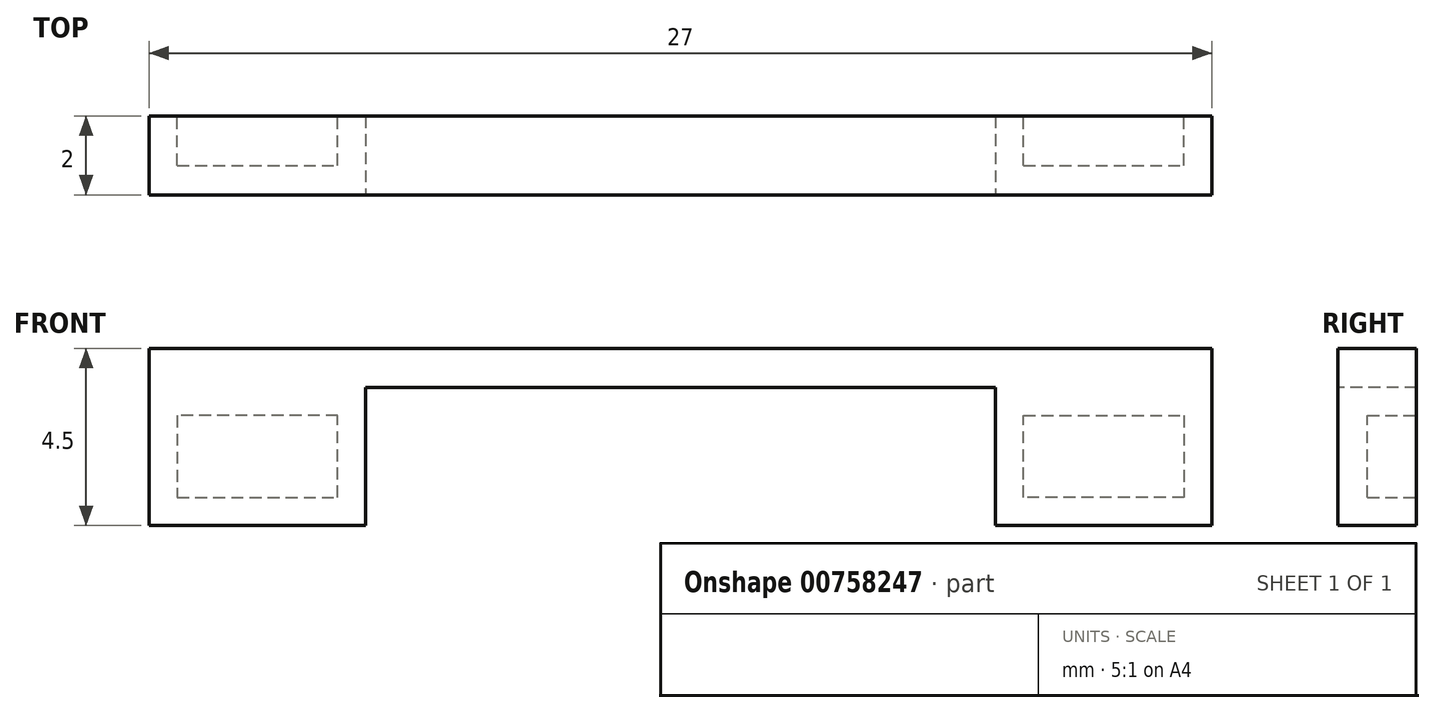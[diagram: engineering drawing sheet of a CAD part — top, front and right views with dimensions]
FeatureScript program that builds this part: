
annotation { "Feature Type Name" : "Feature", "Feature Type Description" : "" }
export const myFeature = defineFeature(function(context is Context, id is Id, definition is map)
    precondition{}
    {
        {
            var Q0;
            Q0=qCreatedBy(makeId("Top.planeOp"),FACE);
            var sketch = newSketch(context, id + "F0", { "sketchPlane" : qUnion([Q0])});
            skLineSegment(sketch, "E0.bottom", {"start": v(-1.02, -0.58) * mm, "end": v(4.48, -0.58) * mm});
            skLineSegment(sketch, "E0.top", {"start": v(-1.02, -2.58) * mm, "end": v(4.48, -2.58) * mm});
            skLineSegment(sketch, "E0.left", {"start": v(-1.02, -0.58) * mm, "end": v(-1.02, -2.58) * mm});
            skLineSegment(sketch, "E0.right", {"start": v(4.48, -0.58) * mm, "end": v(4.48, -2.58) * mm});
            skSolve(sketch);
        }
        {
            var Q0;
            Q0=makeQuery(id+"F0.imprint","IMPRINT",FACE,{"disambiguationData":[TD([[makeQuery(id+"F0.imprint","IMPRINT",EDGE,{"derivedFrom":sQuery(id+"F0.wireOp",EDGE,"E0.bottom")}),-1.0]])]});
            extrude(context, id + "F1", {"entities" : qUnion([Q0]), "depth" : 3.5 * mm, "offsetDistance" : 25 * mm});
        }
        {
            var Q0;
            Q0=makeQuery(id+"F1.opExtrude","SWEPT_FACE",FACE,{"disambiguationData":[OSD([sQuery(id+"F0.wireOp",EDGE,"E0.bottom")])]});
            var sketch = newSketch(context, id + "F2", { "sketchPlane" : qUnion([Q0])});
            skLineSegment(sketch, "E1.0", {"start": v(-3.77, 0.7) * mm, "end": v(0.3, 0.7) * mm});
            skLineSegment(sketch, "E1.1", {"start": v(-3.77, 2.8) * mm, "end": v(-3.77, 0.7) * mm});
            skLineSegment(sketch, "E1.2", {"start": v(0.3, 2.8) * mm, "end": v(-3.77, 2.8) * mm});
            skLineSegment(sketch, "E1.3", {"start": v(0.3, 0.7) * mm, "end": v(0.3, 2.8) * mm});
            skSolve(sketch);
        }
        {
            var Q0;
            Q0=makeQuery(id+"F2.imprint","IMPRINT",FACE,{"disambiguationData":[TD([[makeQuery(id+"F2.imprint","IMPRINT",EDGE,{"derivedFrom":sQuery(id+"F2.wireOp",EDGE,"E1.0")}),1.0]])]});
            var Q1;
            Q1=makeQuery(id+"F1.opExtrude","SWEPT_FACE",FACE,{"disambiguationData":[OSD([sQuery(id+"F0.wireOp",EDGE,"E0.top")])]});
            extrude(context, id + "F3", {"entities" : qUnion([Q0]), "operationType" : NewBodyOperationType.REMOVE, "endBound" : BoundingType.UP_TO_SURFACE, "oppositeDirection" : true, "depth" : 25 * mm, "endBoundEntityFace" : qUnion([Q1]), "hasOffset" : true, "offsetDistance" : 0.75 * mm});
        }
        {
            var Q0;
            Q0=makeQuery(id+"F1.opExtrude","SWEPT_FACE",FACE,{"disambiguationData":[OSD([sQuery(id+"F0.wireOp",EDGE,"E0.bottom")])]});
            var sketch = newSketch(context, id + "F4", { "sketchPlane" : qUnion([Q0])});
            skLineSegment(sketch, "E2", {"start": v(-4.48, 3.5) * mm, "end": v(-4.48, 4.5) * mm});
            skLineSegment(sketch, "E3", {"start": v(-4.48, 4.5) * mm, "end": v(9.02, 4.5) * mm});
            skLineSegment(sketch, "E4", {"start": v(9.02, 4.5) * mm, "end": v(9.02, 3.5) * mm});
            skLineSegment(sketch, "E5", {"start": v(9.02, 3.5) * mm, "end": v(1.02, 3.5) * mm});
            skSolve(sketch);
        }
        {
            var Q0;
            Q0=makeQuery(id+"F4.imprint","IMPRINT",FACE,{"disambiguationData":[TD([[makeQuery(id+"F4.imprint","IMPRINT",EDGE,{"derivedFrom":sQuery(id+"F4.wireOp",EDGE,"E2")}),-1.0]])]});
            var Q1;
            Q1=makeQuery(id+"F1.opExtrude","SWEPT_FACE",FACE,{"disambiguationData":[OSD([sQuery(id+"F0.wireOp",EDGE,"E0.top")])]});
            extrude(context, id + "F5", {"entities" : qUnion([Q0]), "operationType" : NewBodyOperationType.ADD, "endBound" : BoundingType.UP_TO_SURFACE, "oppositeDirection" : true, "depth" : 25 * mm, "endBoundEntityFace" : qUnion([Q1]), "offsetDistance" : 25 * mm});
        }
        {
            var Q0;
            Q0=makeQuery(id+"F1.opExtrude","SWEPT_BODY",BODY,{"disambiguationData":[OSD([sQuery(id+"F0.wireOp",EDGE,"E0.bottom"),sQuery(id+"F0.wireOp",EDGE,"E0.top"),sQuery(id+"F0.wireOp",EDGE,"E0.left"),sQuery(id+"F0.wireOp",EDGE,"E0.right")])]});
            var Q1;
            Q1=makeQuery(id+"F5.opExtrude","SWEPT_FACE",FACE,{"disambiguationData":[OSD([sQuery(id+"F4.wireOp",EDGE,"E4")])]});
            mirror(context, id + "F6", {"operationType" : NewBodyOperationType.ADD, "entities" : qUnion([Q0]), "mirrorPlane" : qUnion([Q1])});
        }
    });
